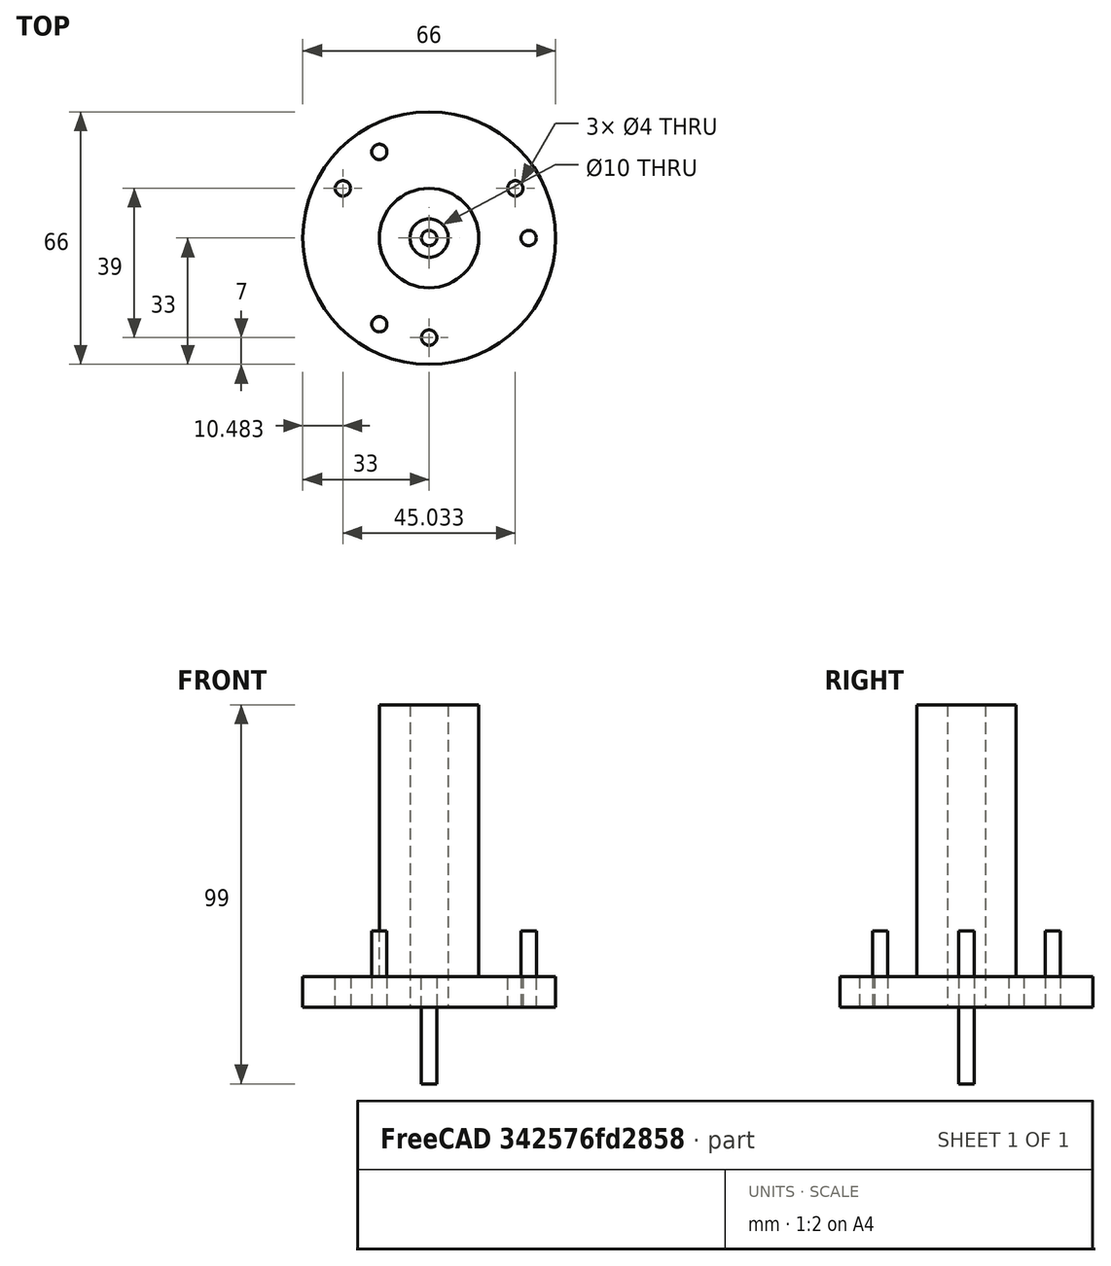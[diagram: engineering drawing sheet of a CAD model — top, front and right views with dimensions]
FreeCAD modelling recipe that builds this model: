
FCSTD DOCUMENT  (FreeCAD 1.1R38827 (Git))
Label: composit_stand3_sleeve_inner_model
License: All rights reserved
LicenseURL: http://en.wikipedia.org/wiki/All_rights_reserved
objects: PartDesign::SubShapeBinder×2, PartDesign::Body×2, PartDesign::Revolution×1, PartDesign::CoordinateSystem×1, Part::Feature×1, App::Link×1, Part::Cylinder×1, Part::FeaturePython×1, Part::MultiFuse×1, PartDesign::Boolean×1
note: 14 computed .brp shape members not serialized (recipe doc carries the construction recipe); baked Part::Feature solids carry a one-line shape summary decoded from their .brp
EXTERNAL_REF file=composit_stand3_sleeve_inner_main.FCStd obj=Sketch
EXTERNAL_REF file=composit_stand3_sleeve_inner_main.FCStd obj=PolarArray

FEATURE [PartDesign::SubShapeBinder] Binder
  BindCopyOnChange = 0
  BindMode = 0
  ClaimChildren = true
  Fuse = false
  MakeFace = true
  OffsetFill = false
  OffsetIntersection = false
  OffsetJoinType = 0
  OffsetOpenResult = false
  PartialLoad = false
  Placement = pos=(0,0,0) rot=(1,0,0;1.5708rad)
  Relative = false
  Support = -> [<external composit_stand3_sleeve_inner_main.FCStd>#Sketch]
  _Version = 2
FEATURE [PartDesign::SubShapeBinder] Binder001
  BindCopyOnChange = 0
  BindMode = 0
  ClaimChildren = true
  Context = -> Body [Binder001.]
  Fuse = false
  MakeFace = true
  OffsetFill = false
  OffsetIntersection = false
  OffsetJoinType = 0
  OffsetOpenResult = false
  PartialLoad = false
  Placement = pos=(0,0,0) rot=(1,0,0;1.5708rad)
  Relative = false
  Support = -> [Binder]
  _Version = 2
FEATURE [PartDesign::Revolution] Revolution
  Angle = 360
  Angle2 = 60
  Axis = (1e-16,1e-16,1)
  Base = (0,0,0)
  Placement = pos=(0,0,0) rot=(1,0,0;1.5708rad)
  Profile = -> Binder001 [Face1]
  ReferenceAxis = -> Z_Axis
  Reversed = true
  Suppressed = false
  Type = 0
FEATURE [PartDesign::CoordinateSystem] Local_CS
  AttacherType = Attacher::AttachEngine3D
  AttachmentOffset = pos=(0,0,8) rot=(0,0,1;0rad)
  AttachmentSupport = -> [XY_Plane]
  MapMode = 5
  Placement = pos=(0,0,8) rot=(0,0,1;0rad)
  expr: .AttachmentOffset.Base.z = <<composit_stand3_sleeve_inner_main>>#<<sleeve_inner_base_sketch>>.Constraints.base_height
FEATURE [Part::Feature] Body169  label="sleeve_inner002"
  shape: bbox 66 x 66 x 79 mm, 9 faces (baked)
FEATURE [App::Link] Link  label="PolarArray"
  LinkTransform = true
  LinkedObject = -> <external composit_stand3_sleeve_inner_main.FCStd>#PolarArray
FEATURE [Part::Cylinder] Cylinder
  Angle = 360
  AttacherType = Attacher::AttachEngine3D
  FirstAngle = 0
  Height = 20
  Placement = pos=(0,0,0) rot=(1,0,0;3.14159rad)
  Radius = 2
  SecondAngle = 0
FEATURE [Part::FeaturePython] Populate  label="Populate PolarArray with Cylinder"  # WARN: FeaturePython — macro-defined, semantics opaque (R4)
  Copying = 0
  ExposePlacement = false
  MarkerShape = 1
  MarkerSize = 0
  NumElements = 0
  Object = -> Cylinder
  OutputCompounding = 1
  PlacementsTo = -> Link
  Referencing = 0
  Type = lattice2PopulateCopies.LatticePopulateCopies
  isLattice = 0
FEATURE [PartDesign::Body] Body170  label="Body"
  AllowCompound = false
  Origin = -> Origin001
FEATURE [Part::MultiFuse] Fusion
  Shapes = -> [Populate]
FEATURE [PartDesign::Boolean] Boolean
  BaseFeature = -> Revolution
  Group = -> [Fusion]
  Suppressed = false
  Type = 1
  UsePlacement = true
FEATURE [PartDesign::Body] Body  label="sleeve_inner"
  AllowCompound = false
  Group = -> [Binder001,Revolution,Local_CS,Boolean]
  Origin = -> Origin
  Tip = -> Boolean
